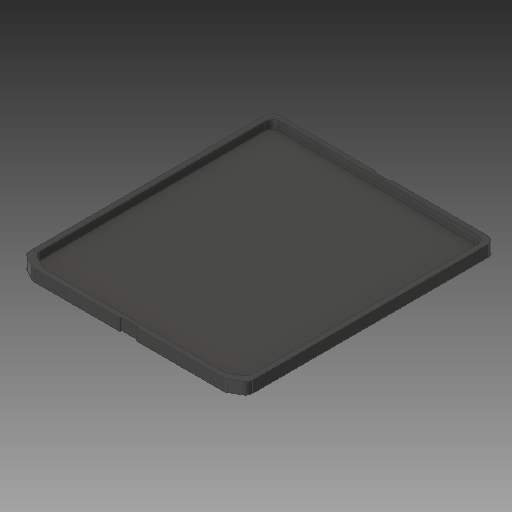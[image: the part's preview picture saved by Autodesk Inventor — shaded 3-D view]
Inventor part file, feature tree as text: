
AUTODESK INVENTOR PART (.ipt)
format: ipt  version: 2019.3 (Build 233278000, 278)  size: 1,131,520 bytes
history: native  units: mm
features: other x9, extrude x4, sketch x2, emboss x1, projected_geometry x1
ambient origin geometry x8: Origin, YZ Plane, XZ Plane, XY Plane, X Axis, Y Axis, Z Axis, Center Point
bodies: Solid3 (feature_tree), Solid2 (feature_tree)
feature tree (17):
  other  "Housing Box 1.ipt"
  sketch  "Sketch3"  dims[d18=10.0mm d19=1.95mm d20=0.0mm]
  extrude  "Extrusion4"  Depth=10.0mm TaperAngle=0.0deg
  extrude  "Extrusion5"  Depth=0.1mm
  extrude  "Extrusion6"  Depth=0.1mm
  extrude  "Extrusion7"  Depth=0.1mm
  emboss  "Emboss1"
  other  "Solid2::Housing Box 1.ipt"
  other  "TaggingFeature1"
  other  "MOTOR1_3"
  other  "MOTOR1_2"
  other  "MOTOR1_1"
  other  "MOTOR2_3"
  other  "MOTOR2_2"
  other  "MOTOR2_1"
  projected_geometry  "Projected Loop1"
  sketch  "Sketch4"  dims[d21=4.9mm d22=0.0mm d23=250.0mm d24=62.565836mm d25=62.565836mm d26=10.0mm d27=1.0mm d28=10.0mm d29=1.0mm d30=10.0mm d31=0.0mm d32=10.0mm d33=0.0mm d34=180.0mm d35=0.1mm d36=0.0mm]
